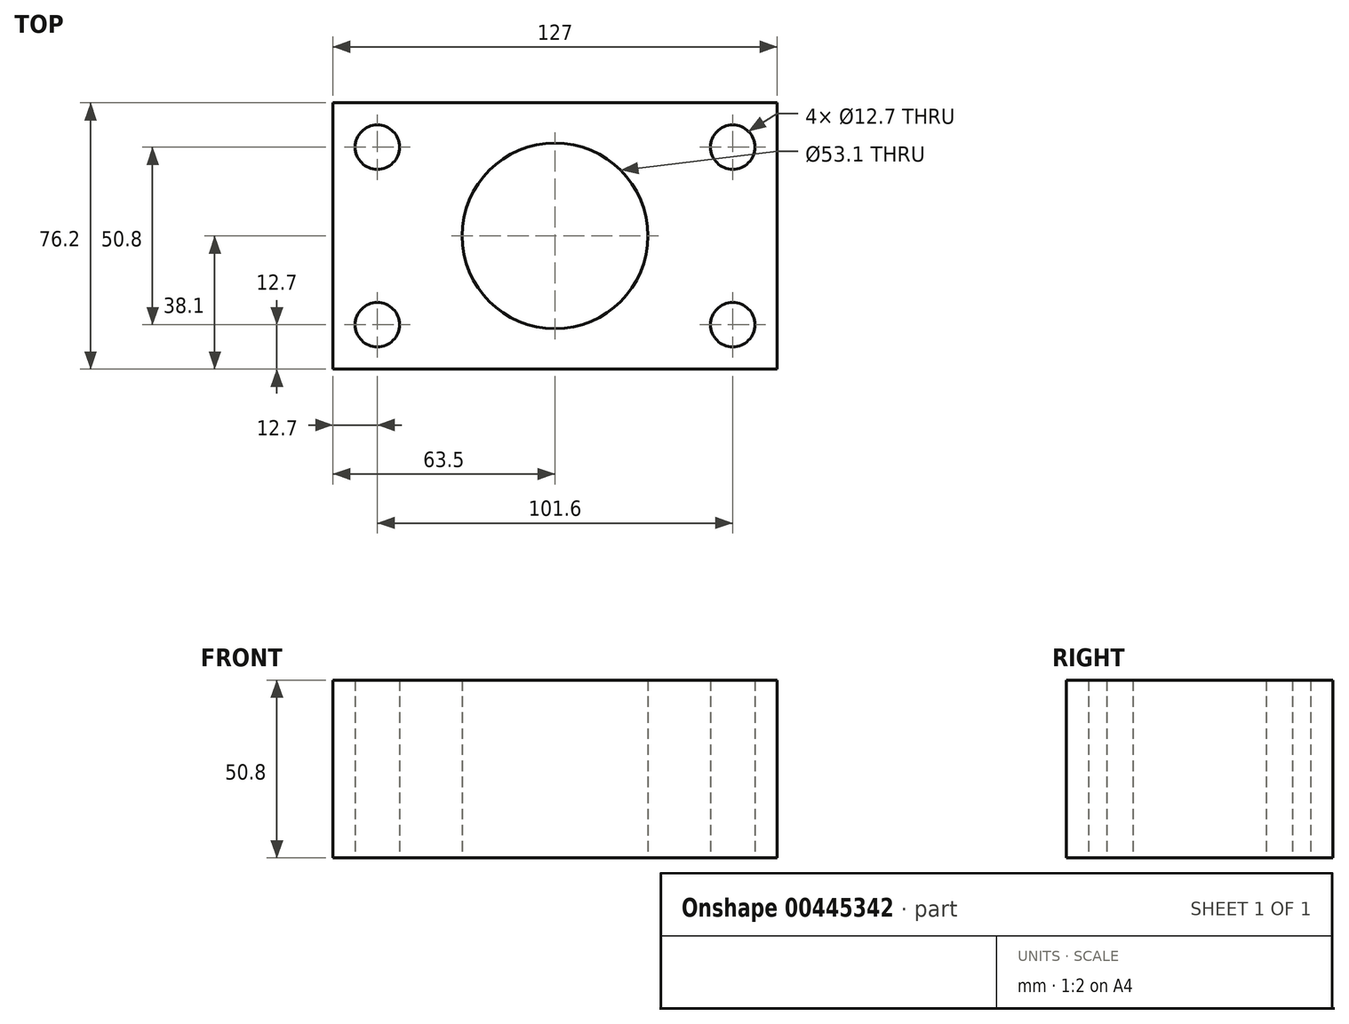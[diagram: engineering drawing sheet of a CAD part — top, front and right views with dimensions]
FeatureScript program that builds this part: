
annotation { "Feature Type Name" : "Feature", "Feature Type Description" : "" }
export const myFeature = defineFeature(function(context is Context, id is Id, definition is map)
    precondition{}
    {
        {
            var Q0;
            Q0=qCreatedBy(makeId("Top.planeOp"),FACE);
            var sketch = newSketch(context, id + "F0", { "sketchPlane" : qUnion([Q0])});
            skLineSegment(sketch, "E0.bottom", {"start": v(63.5, 38.1) * mm, "end": v(-63.5, 38.1) * mm});
            skLineSegment(sketch, "E0.top", {"start": v(63.5, -38.1) * mm, "end": v(-63.5, -38.1) * mm});
            skLineSegment(sketch, "E0.left", {"start": v(63.5, 38.1) * mm, "end": v(63.5, -38.1) * mm});
            skLineSegment(sketch, "E0.right", {"start": v(-63.5, 38.1) * mm, "end": v(-63.5, -38.1) * mm});
            skPoint(sketch, "E0.middle", {"position": v(0, 0) * mm});
            skCircle(sketch, "E1", {"center": v(-50.8, 25.4) * mm, "radius": 6.35 * mm});
            skCircle(sketch, "E2", {"center": v(-50.8, -25.4) * mm, "radius": 6.35 * mm});
            skCircle(sketch, "E3", {"center": v(50.8, 25.4) * mm, "radius": 6.35 * mm});
            skCircle(sketch, "E4", {"center": v(50.8, -25.4) * mm, "radius": 6.35 * mm});
            skSolve(sketch);
        }
        {
            var Q0;
            Q0=makeQuery(id+"F0.imprint","IMPRINT",FACE,{"disambiguationData":[TD([[makeQuery(id+"F0.imprint","IMPRINT",EDGE,{"derivedFrom":sQuery(id+"F0.wireOp",EDGE,"E0.bottom")}),1.0]])]});
            extrude(context, id + "F1", {"entities" : qUnion([Q0]), "depth" : 50.8 * mm});
        }
        {
            var Q0;
            Q0=qCreatedBy(makeId("Top.planeOp"),FACE);
            var sketch = newSketch(context, id + "F2", { "sketchPlane" : qUnion([Q0])});
            skCircle(sketch, "E5", {"center": v(0, 0) * mm, "radius": 26.55 * mm});
            skSolve(sketch);
        }
        {
            var Q0;
            Q0 = qSketchRegion(id + "F2", true);
            extrude(context, id + "F3", {"entities" : qUnion([Q0]), "operationType" : NewBodyOperationType.REMOVE, "endBound" : BoundingType.THROUGH_ALL, "depth" : 25.4 * mm});
        }
    });
